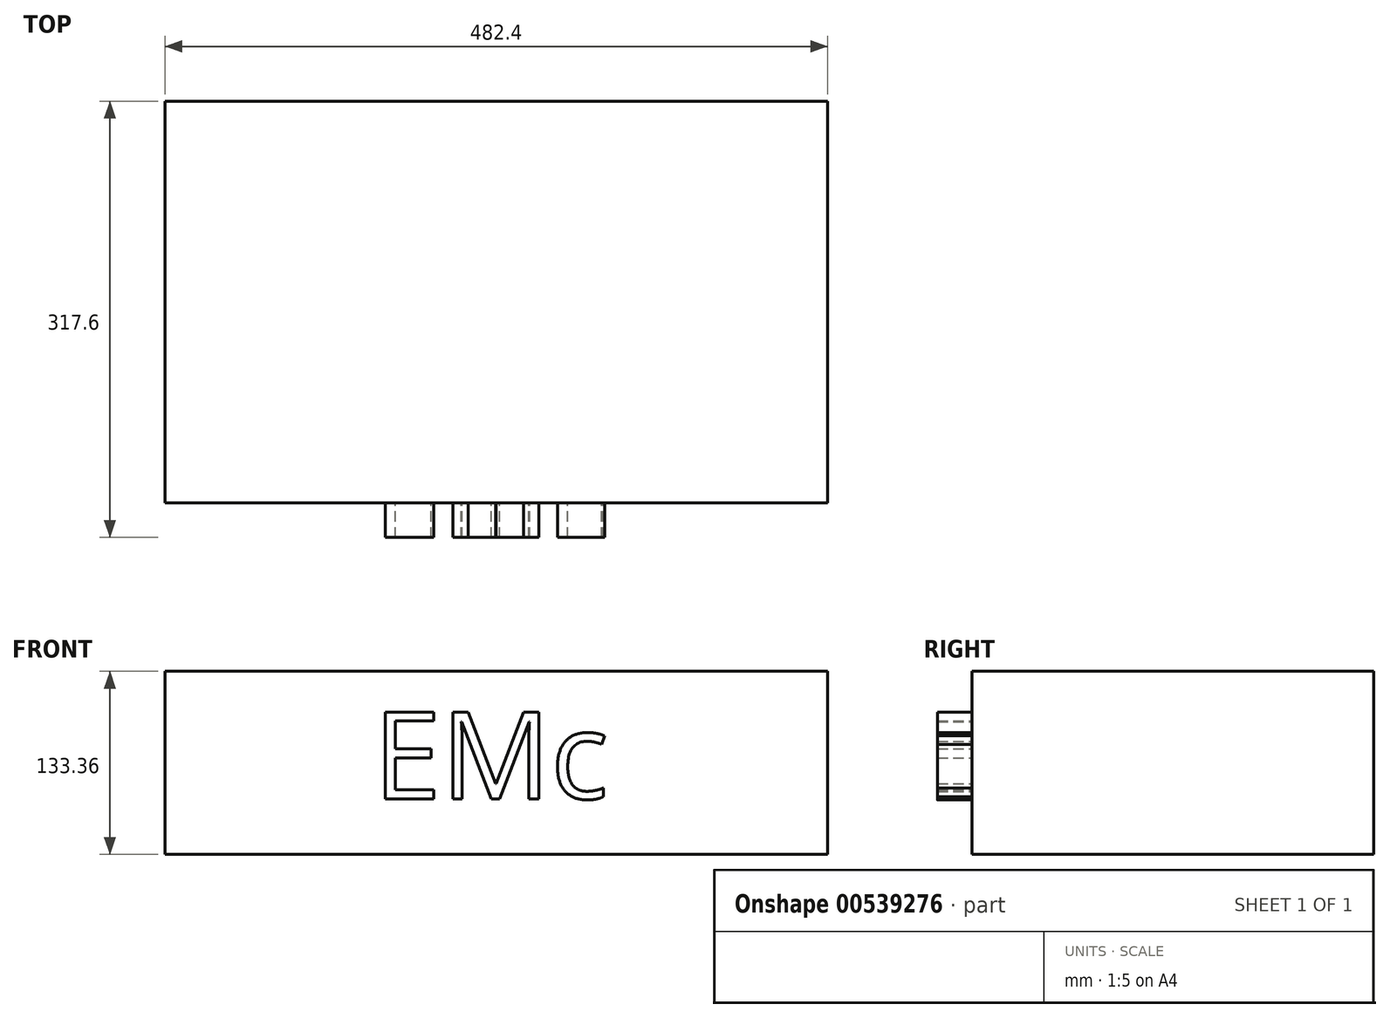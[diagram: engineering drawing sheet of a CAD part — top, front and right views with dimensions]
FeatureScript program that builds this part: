
annotation { "Feature Type Name" : "Feature", "Feature Type Description" : "" }
export const myFeature = defineFeature(function(context is Context, id is Id, definition is map)
    precondition{}
    {
        {
            var Q0;
            Q0=qCreatedBy(makeId("Front.planeOp"),FACE);
            var sketch = newSketch(context, id + "F0", { "sketchPlane" : qUnion([Q0])});
            skLineSegment(sketch, "E0.bottom", {"start": v(-241.2, -66.67) * mm, "end": v(241.2, -66.67) * mm});
            skLineSegment(sketch, "E0.top", {"start": v(-241.2, 66.68) * mm, "end": v(241.2, 66.68) * mm});
            skLineSegment(sketch, "E0.left", {"start": v(-241.2, -66.67) * mm, "end": v(-241.2, 66.68) * mm});
            skLineSegment(sketch, "E0.right", {"start": v(241.2, -66.67) * mm, "end": v(241.2, 66.68) * mm});
            skPoint(sketch, "E0.middle", {"position": v(0, 0) * mm});
            skSolve(sketch);
        }
        {
            var Q0;
            Q0=makeQuery(id+"F0.imprint","IMPRINT",FACE,{"disambiguationData":[TD([[makeQuery(id+"F0.imprint","IMPRINT",EDGE,{"derivedFrom":sQuery(id+"F0.wireOp",EDGE,"E0.bottom")}),1.0]])]});
            extrude(context, id + "F1", {"entities" : qUnion([Q0]), "depth" : 292.6 * mm, "offsetDistance" : 25 * mm});
        }
        {
            var Q0;
            Q0=makeQuery(id+"F1.opExtrude","CAP_FACE",FACE,{"disambiguationData":[OSD([sQuery(id+"F0.wireOp",EDGE,"E0.bottom"),sQuery(id+"F0.wireOp",EDGE,"E0.top"),sQuery(id+"F0.wireOp",EDGE,"E0.left"),sQuery(id+"F0.wireOp",EDGE,"E0.right")])],"isStart":false});
            var sketch = newSketch(context, id + "F2", { "sketchPlane" : qUnion([Q0])});
            skText(sketch, "E1", { "text": "EMc", "fontName": "OpenSans-Regular.ttf"});
            const initialGuessF2  = {"E1": [-0.08951, -0.02615, 1, 0, 0.06373]};
            skSetInitialGuess(sketch, initialGuessF2);
            skSolve(sketch);
        }
        {
            var Q0;
            Q0 = qSketchRegion(id + "F2", true);
            extrude(context, id + "F3", {"entities" : qUnion([Q0]), "operationType" : NewBodyOperationType.ADD, "depth" : 25 * mm, "offsetDistance" : 25 * mm});
        }
    });
